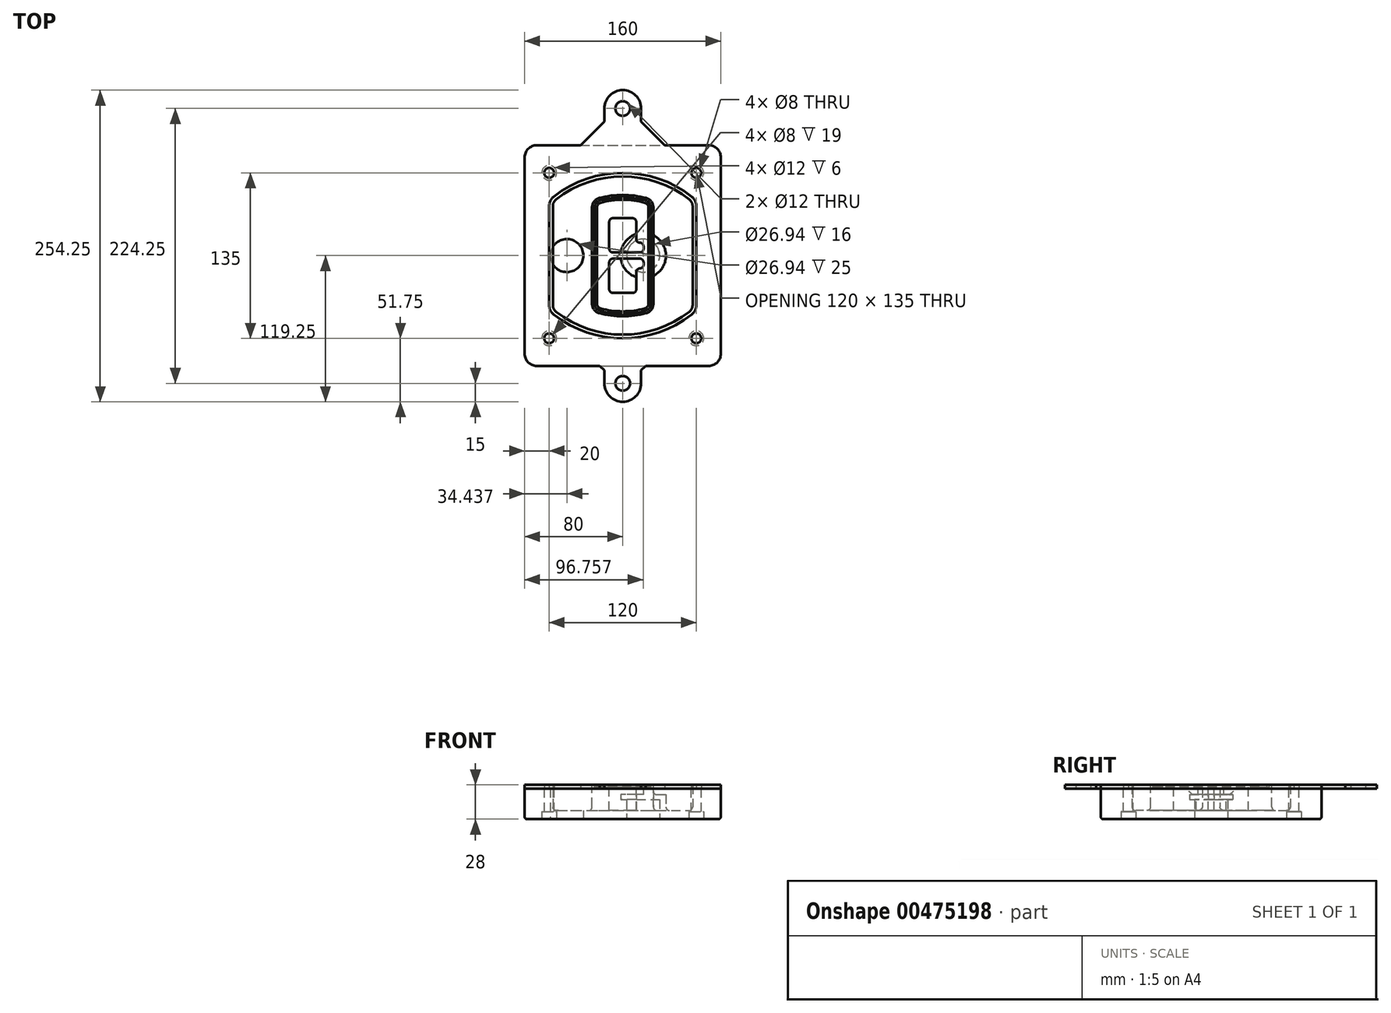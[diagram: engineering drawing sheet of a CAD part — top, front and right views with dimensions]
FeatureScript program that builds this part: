
annotation { "Feature Type Name" : "Feature", "Feature Type Description" : "" }
export const myFeature = defineFeature(function(context is Context, id is Id, definition is map)
    precondition{}
    {
        {
            var Q0;
            Q0=qCreatedBy(makeId("Top.planeOp"),FACE);
            var sketch = newSketch(context, id + "F0", { "sketchPlane" : qUnion([Q0])});
            skPoint(sketch, "E0.rect.middle", {"position": v(0, 0) * mm});
            skLineSegment(sketch, "E1.bottom", {"start": v(-70, -90) * mm, "end": v(70, -90) * mm});
            skLineSegment(sketch, "E1.top", {"start": v(-70, 90) * mm, "end": v(70, 90) * mm});
            skLineSegment(sketch, "E1.left", {"start": v(-80, -80) * mm, "end": v(-80, 80) * mm});
            skLineSegment(sketch, "E1.right", {"start": v(80, -80) * mm, "end": v(80, 80) * mm});
            skLineSegment(sketch, "E2", {"start": v(-80, 90) * mm, "end": v(80, -90) * mm, "construction": true});
            skLineSegment(sketch, "E3", {"start": v(80, 90) * mm, "end": v(-80, -90) * mm, "construction": true});
            skCircle(sketch, "E4", {"center": v(-60, 67.5) * mm, "radius": 4 * mm});
            skCircle(sketch, "E5", {"center": v(60, 67.5) * mm, "radius": 4 * mm});
            skCircle(sketch, "E6", {"center": v(60, -67.5) * mm, "radius": 4 * mm});
            skCircle(sketch, "E7", {"center": v(-60, -67.5) * mm, "radius": 4 * mm});
            skLineSegment(sketch, "E8", {"start": v(-60, 67.5) * mm, "end": v(60, 67.5) * mm, "construction": true});
            skLineSegment(sketch, "E9", {"start": v(60, 67.5) * mm, "end": v(60, -67.5) * mm, "construction": true});
            skLineSegment(sketch, "E10", {"start": v(60, -67.5) * mm, "end": v(-60, -67.5) * mm, "construction": true});
            skLineSegment(sketch, "E11", {"start": v(-60, -67.5) * mm, "end": v(-60, 67.5) * mm, "construction": true});
            skLineSegment(sketch, "E12", {"start": v(-60, 40.3) * mm, "end": v(-60, -40.3) * mm});
            skLineSegment(sketch, "E13", {"start": v(60, 40.3) * mm, "end": v(60, -40.3) * mm});
            skArc(sketch, "E14", {"start": v(56.15, 48.18) * mm, "mid": v(0, 67.5) * mm, "end": v(-56.15, 48.18) * mm});
            skArc(sketch, "E15", {"start": v(-56.15, -48.18) * mm, "mid": v(0, -67.5) * mm, "end": v(56.15, -48.18) * mm});
            skLineSegment(sketch, "E16", {"start": v(-60, 0) * mm, "end": v(60, 0) * mm, "construction": true});
            skPoint(sketch, "E17.visualSharp", {"position": v(-60, -45) * mm});
            skArc(sketch, "E17.filletArc", {"start": v(-60, -40.3) * mm, "mid": v(-58.99, -44.68) * mm, "end": v(-56.15, -48.18) * mm});
            skPoint(sketch, "E18.visualSharp", {"position": v(-60, 45) * mm});
            skArc(sketch, "E18.filletArc", {"start": v(-56.15, 48.18) * mm, "mid": v(-58.99, 44.68) * mm, "end": v(-60, 40.3) * mm});
            skPoint(sketch, "E19.visualSharp", {"position": v(60, 45) * mm});
            skArc(sketch, "E19.filletArc", {"start": v(60, 40.3) * mm, "mid": v(58.99, 44.68) * mm, "end": v(56.15, 48.18) * mm});
            skPoint(sketch, "E20.visualSharp", {"position": v(60, -45) * mm});
            skArc(sketch, "E20.filletArc", {"start": v(56.15, -48.18) * mm, "mid": v(58.99, -44.68) * mm, "end": v(60, -40.3) * mm});
            skPoint(sketch, "E21.visualSharp", {"position": v(-80, 90) * mm});
            skArc(sketch, "E21.filletArc", {"start": v(-70, 90) * mm, "mid": v(-77.07, 87.07) * mm, "end": v(-80, 80) * mm});
            skPoint(sketch, "E22.visualSharp", {"position": v(80, 90) * mm});
            skArc(sketch, "E22.filletArc", {"start": v(80, 80) * mm, "mid": v(77.07, 87.07) * mm, "end": v(70, 90) * mm});
            skPoint(sketch, "E23.visualSharp", {"position": v(80, -90) * mm});
            skArc(sketch, "E23.filletArc", {"start": v(70, -90) * mm, "mid": v(77.07, -87.07) * mm, "end": v(80, -80) * mm});
            skPoint(sketch, "E24.visualSharp", {"position": v(-80, -90) * mm});
            skArc(sketch, "E24.filletArc", {"start": v(-80, -80) * mm, "mid": v(-77.07, -87.07) * mm, "end": v(-70, -90) * mm});
            skArc(sketch, "E25.0", {"start": v(57, 40.3) * mm, "mid": v(56.3, 43.36) * mm, "end": v(54.3, 45.81) * mm});
            skLineSegment(sketch, "E25.1", {"start": v(57, 40.3) * mm, "end": v(57, -40.3) * mm});
            skArc(sketch, "E25.2", {"start": v(54.3, -45.81) * mm, "mid": v(56.3, -43.36) * mm, "end": v(57, -40.3) * mm});
            skArc(sketch, "E25.3", {"start": v(-54.3, -45.81) * mm, "mid": v(0, -64.5) * mm, "end": v(54.3, -45.81) * mm});
            skArc(sketch, "E25.4", {"start": v(-57, -40.3) * mm, "mid": v(-56.3, -43.36) * mm, "end": v(-54.3, -45.81) * mm});
            skArc(sketch, "E25.5", {"start": v(54.3, 45.81) * mm, "mid": v(0, 64.5) * mm, "end": v(-54.3, 45.81) * mm});
            skLineSegment(sketch, "E25.6", {"start": v(-57, 40.3) * mm, "end": v(-57, -40.3) * mm});
            skArc(sketch, "E25.7", {"start": v(-54.3, 45.81) * mm, "mid": v(-56.3, 43.36) * mm, "end": v(-57, 40.3) * mm});
            skArc(sketch, "E26.0", {"start": v(-58.62, 51.33) * mm, "mid": v(-62.58, 46.43) * mm, "end": v(-64, 40.3) * mm});
            skArc(sketch, "E26.1", {"start": v(58.62, 51.33) * mm, "mid": v(0, 71.5) * mm, "end": v(-58.62, 51.33) * mm});
            skArc(sketch, "E26.2", {"start": v(64, 40.3) * mm, "mid": v(62.58, 46.43) * mm, "end": v(58.62, 51.33) * mm});
            skLineSegment(sketch, "E26.3", {"start": v(64, 40.3) * mm, "end": v(64, -40.3) * mm});
            skArc(sketch, "E26.4", {"start": v(58.62, -51.33) * mm, "mid": v(62.58, -46.43) * mm, "end": v(64, -40.3) * mm});
            skLineSegment(sketch, "E26.5", {"start": v(-64, 40.3) * mm, "end": v(-64, -40.3) * mm});
            skArc(sketch, "E26.6", {"start": v(-58.62, -51.33) * mm, "mid": v(0, -71.5) * mm, "end": v(58.62, -51.33) * mm});
            skArc(sketch, "E26.7", {"start": v(-64, -40.3) * mm, "mid": v(-62.58, -46.43) * mm, "end": v(-58.62, -51.33) * mm});
            skSolve(sketch);
        }
        {
            var Q0;
            Q0=makeQuery(id+"F0.imprint","IMPRINT",FACE,{"disambiguationData":[TD([[makeQuery(id+"F0.imprint","IMPRINT",EDGE,{"derivedFrom":sQuery(id+"F0.wireOp",EDGE,"E1.bottom")}),1.0]])]});
            var Q1;
            Q1=makeQuery(id+"F0.imprint","IMPRINT",FACE,{"disambiguationData":[TD([[makeQuery(id+"F0.imprint","IMPRINT",EDGE,{"derivedFrom":sQuery(id+"F0.wireOp",EDGE,"E12")}),1.0]])]});
            var Q2;
            Q2=makeQuery(id+"F0.imprint","IMPRINT",FACE,{"disambiguationData":[TD([[makeQuery(id+"F0.imprint","IMPRINT",EDGE,{"derivedFrom":sQuery(id+"F0.wireOp",EDGE,"E25.0")}),1.0]])]});
            var Q3;
            Q3=makeQuery(id+"F0.imprint","IMPRINT",FACE,{"disambiguationData":[TD([[makeQuery(id+"F0.imprint","IMPRINT",EDGE,{"derivedFrom":sQuery(id+"F0.wireOp",EDGE,"E12")}),-1.0]])]});
            extrude(context, id + "F1", {"entities" : qUnion([Q0, Q1, Q2, Q3]), "oppositeDirection" : true, "depth" : 25 * mm});
        }
        {
            var Q0;
            Q0=makeQuery(id+"F0.imprint","IMPRINT",FACE,{"disambiguationData":[TD([[makeQuery(id+"F0.imprint","IMPRINT",EDGE,{"derivedFrom":sQuery(id+"F0.wireOp",EDGE,"E12")}),1.0]])]});
            extrude(context, id + "F2", {"entities" : qUnion([Q0]), "operationType" : NewBodyOperationType.ADD, "depth" : 3 * mm});
        }
        {
            var Q0;
            Q0=makeQuery(id+"F0.imprint","IMPRINT",FACE,{"disambiguationData":[TD([[makeQuery(id+"F0.imprint","IMPRINT",EDGE,{"derivedFrom":sQuery(id+"F0.wireOp",EDGE,"E25.0")}),1.0]])]});
            extrude(context, id + "F3", {"entities" : qUnion([Q0]), "operationType" : NewBodyOperationType.REMOVE, "oppositeDirection" : true, "depth" : 18 * mm});
        }
        {
            var Q0;
            Q0=makeQuery(id+"F2.opExtrude","CAP_FACE",FACE,{"disambiguationData":[OSD([sQuery(id+"F0.wireOp",EDGE,"E12"),sQuery(id+"F0.wireOp",EDGE,"E13"),sQuery(id+"F0.wireOp",EDGE,"E14"),sQuery(id+"F0.wireOp",EDGE,"E15"),sQuery(id+"F0.wireOp",EDGE,"E17.filletArc"),sQuery(id+"F0.wireOp",EDGE,"E18.filletArc"),sQuery(id+"F0.wireOp",EDGE,"E19.filletArc"),sQuery(id+"F0.wireOp",EDGE,"E20.filletArc"),sQuery(id+"F0.wireOp",EDGE,"E25.0"),sQuery(id+"F0.wireOp",EDGE,"E25.1"),sQuery(id+"F0.wireOp",EDGE,"E25.2"),sQuery(id+"F0.wireOp",EDGE,"E25.3"),sQuery(id+"F0.wireOp",EDGE,"E25.4"),sQuery(id+"F0.wireOp",EDGE,"E25.5"),sQuery(id+"F0.wireOp",EDGE,"E25.6"),sQuery(id+"F0.wireOp",EDGE,"E25.7")])],"isStart":false});
            var sketch = newSketch(context, id + "F4", { "sketchPlane" : qUnion([Q0])});
            skArc(sketch, "E27.0", {"start": v(-19.08, -46.97) * mm, "mid": v(0, -49.5) * mm, "end": v(19.08, -46.97) * mm});
            skArc(sketch, "E28.0", {"start": v(19.08, 46.97) * mm, "mid": v(0, 49.5) * mm, "end": v(-19.08, 46.97) * mm});
            skLineSegment(sketch, "E29", {"start": v(-25, 39.25) * mm, "end": v(-25, -39.25) * mm});
            skLineSegment(sketch, "E30", {"start": v(25, 39.25) * mm, "end": v(25, -39.25) * mm});
            skLineSegment(sketch, "E31", {"start": v(-25, 45.1) * mm, "end": v(25, 45.1) * mm, "construction": true});
            skLineSegment(sketch, "E32", {"start": v(-25, -45.1) * mm, "end": v(25, -45.1) * mm, "construction": true});
            skPoint(sketch, "E33.visualSharp", {"position": v(-25, 45.1) * mm});
            skArc(sketch, "E33.filletArc", {"start": v(-19.08, 46.97) * mm, "mid": v(-23.35, 44.11) * mm, "end": v(-25, 39.25) * mm});
            skPoint(sketch, "E34.visualSharp", {"position": v(25, 45.1) * mm});
            skArc(sketch, "E34.filletArc", {"start": v(25, 39.25) * mm, "mid": v(23.35, 44.11) * mm, "end": v(19.08, 46.97) * mm});
            skPoint(sketch, "E35.visualSharp", {"position": v(25, -45.1) * mm});
            skArc(sketch, "E35.filletArc", {"start": v(19.08, -46.97) * mm, "mid": v(23.35, -44.11) * mm, "end": v(25, -39.25) * mm});
            skPoint(sketch, "E36.visualSharp", {"position": v(-25, -45.1) * mm});
            skArc(sketch, "E36.filletArc", {"start": v(-25, -39.25) * mm, "mid": v(-23.35, -44.11) * mm, "end": v(-19.08, -46.97) * mm});
            skArc(sketch, "E37.0", {"start": v(54.3, 45.81) * mm, "mid": v(0, 64.5) * mm, "end": v(-54.3, 45.81) * mm});
            skArc(sketch, "E37.1", {"start": v(-54.3, 45.81) * mm, "mid": v(-56.3, 43.36) * mm, "end": v(-57, 40.3) * mm});
            skLineSegment(sketch, "E37.2", {"start": v(-57, 40.3) * mm, "end": v(-57, -40.3) * mm});
            skArc(sketch, "E37.3", {"start": v(-57, -40.3) * mm, "mid": v(-56.3, -43.36) * mm, "end": v(-54.3, -45.81) * mm});
            skArc(sketch, "E37.4", {"start": v(-54.3, -45.81) * mm, "mid": v(0, -64.5) * mm, "end": v(54.3, -45.81) * mm});
            skArc(sketch, "E37.5", {"start": v(54.3, -45.81) * mm, "mid": v(56.3, -43.36) * mm, "end": v(57, -40.3) * mm});
            skLineSegment(sketch, "E37.6", {"start": v(57, 40.3) * mm, "end": v(57, -40.3) * mm});
            skArc(sketch, "E37.7", {"start": v(57, 40.3) * mm, "mid": v(56.3, 43.36) * mm, "end": v(54.3, 45.81) * mm});
            skLineSegment(sketch, "E38.0", {"start": v(23, 39.25) * mm, "end": v(23, -39.25) * mm});
            skArc(sketch, "E38.1", {"start": v(18.56, -45.04) * mm, "mid": v(21.76, -42.9) * mm, "end": v(23, -39.25) * mm});
            skArc(sketch, "E38.2", {"start": v(-18.56, -45.04) * mm, "mid": v(0, -47.5) * mm, "end": v(18.56, -45.04) * mm});
            skArc(sketch, "E38.3", {"start": v(-23, -39.25) * mm, "mid": v(-21.76, -42.9) * mm, "end": v(-18.56, -45.04) * mm});
            skLineSegment(sketch, "E38.4", {"start": v(-23, 39.25) * mm, "end": v(-23, -39.25) * mm});
            skArc(sketch, "E38.5", {"start": v(23, 39.25) * mm, "mid": v(21.76, 42.9) * mm, "end": v(18.56, 45.04) * mm});
            skArc(sketch, "E38.6", {"start": v(-18.56, 45.04) * mm, "mid": v(-21.76, 42.9) * mm, "end": v(-23, 39.25) * mm});
            skArc(sketch, "E38.7", {"start": v(18.56, 45.04) * mm, "mid": v(0, 47.5) * mm, "end": v(-18.56, 45.04) * mm});
            skArc(sketch, "E39.0", {"start": v(21, 39.25) * mm, "mid": v(20.18, 41.68) * mm, "end": v(18.04, 43.1) * mm});
            skLineSegment(sketch, "E39.1", {"start": v(21, 39.25) * mm, "end": v(21, -39.25) * mm});
            skArc(sketch, "E39.2", {"start": v(18.04, -43.1) * mm, "mid": v(20.18, -41.68) * mm, "end": v(21, -39.25) * mm});
            skArc(sketch, "E39.3", {"start": v(-18.04, -43.1) * mm, "mid": v(0, -45.5) * mm, "end": v(18.04, -43.1) * mm});
            skArc(sketch, "E39.4", {"start": v(-21, -39.25) * mm, "mid": v(-20.18, -41.68) * mm, "end": v(-18.04, -43.1) * mm});
            skArc(sketch, "E39.5", {"start": v(18.04, 43.1) * mm, "mid": v(0, 45.5) * mm, "end": v(-18.04, 43.1) * mm});
            skLineSegment(sketch, "E39.6", {"start": v(-21, 39.25) * mm, "end": v(-21, -39.25) * mm});
            skArc(sketch, "E39.7", {"start": v(-18.04, 43.1) * mm, "mid": v(-20.18, 41.68) * mm, "end": v(-21, 39.25) * mm});
            skLineSegment(sketch, "E40", {"start": v(-25, 0) * mm, "end": v(25, 0) * mm, "construction": true});
            skLineSegment(sketch, "E41", {"start": v(-11, 5.5) * mm, "end": v(-11, 27.5) * mm});
            skLineSegment(sketch, "E42", {"start": v(-8, 30.5) * mm, "end": v(8, 30.5) * mm});
            skLineSegment(sketch, "E43", {"start": v(11, 27.5) * mm, "end": v(11, 13.5) * mm});
            skLineSegment(sketch, "E44", {"start": v(14, 10.5) * mm, "end": v(14, 10.5) * mm});
            skLineSegment(sketch, "E45", {"start": v(17, 7.5) * mm, "end": v(17, 5.5) * mm});
            skLineSegment(sketch, "E46", {"start": v(14, 2.5) * mm, "end": v(-8, 2.5) * mm});
            skPoint(sketch, "E47.visualSharp", {"position": v(-11, 30.5) * mm});
            skArc(sketch, "E47.filletArc", {"start": v(-8, 30.5) * mm, "mid": v(-10.12, 29.62) * mm, "end": v(-11, 27.5) * mm});
            skPoint(sketch, "E48.visualSharp", {"position": v(11, 30.5) * mm});
            skArc(sketch, "E48.filletArc", {"start": v(11, 27.5) * mm, "mid": v(10.12, 29.62) * mm, "end": v(8, 30.5) * mm});
            skPoint(sketch, "E49.visualSharp", {"position": v(11, 10.5) * mm});
            skArc(sketch, "E49.filletArc", {"start": v(11, 13.5) * mm, "mid": v(11.88, 11.38) * mm, "end": v(14, 10.5) * mm});
            skPoint(sketch, "E50.visualSharp", {"position": v(17, 10.5) * mm});
            skArc(sketch, "E50.filletArc", {"start": v(17, 7.5) * mm, "mid": v(16.12, 9.62) * mm, "end": v(14, 10.5) * mm});
            skPoint(sketch, "E51.visualSharp", {"position": v(17, 2.5) * mm});
            skArc(sketch, "E51.filletArc", {"start": v(14, 2.5) * mm, "mid": v(16.12, 3.38) * mm, "end": v(17, 5.5) * mm});
            skPoint(sketch, "E52.visualSharp", {"position": v(-11, 2.5) * mm});
            skArc(sketch, "E52.filletArc", {"start": v(-11, 5.5) * mm, "mid": v(-10.12, 3.38) * mm, "end": v(-8, 2.5) * mm});
            skLineSegment(sketch, "E53.0.MirrorCS", {"start": v(14, -2.5) * mm, "end": v(-8, -2.5) * mm});
            skArc(sketch, "E54.0.MirrorCS", {"start": v(-11, -5.5) * mm, "mid": v(-10.12, -3.38) * mm, "end": v(-8, -2.5) * mm});
            skLineSegment(sketch, "E55.0.MirrorCS", {"start": v(-11, -5.5) * mm, "end": v(-11, -27.5) * mm});
            skArc(sketch, "E56.0.MirrorCS", {"start": v(-8, -30.5) * mm, "mid": v(-10.12, -29.62) * mm, "end": v(-11, -27.5) * mm});
            skLineSegment(sketch, "E57.0.MirrorCS", {"start": v(-8, -30.5) * mm, "end": v(8, -30.5) * mm});
            skArc(sketch, "E58.0.MirrorCS", {"start": v(11, -27.5) * mm, "mid": v(10.12, -29.62) * mm, "end": v(8, -30.5) * mm});
            skLineSegment(sketch, "E59.0.MirrorCS", {"start": v(11, -27.5) * mm, "end": v(11, -13.5) * mm});
            skArc(sketch, "E60.0.MirrorCS", {"start": v(11, -13.5) * mm, "mid": v(11.88, -11.38) * mm, "end": v(14, -10.5) * mm});
            skArc(sketch, "E61.0.MirrorCS", {"start": v(17, -7.5) * mm, "mid": v(16.12, -9.62) * mm, "end": v(14, -10.5) * mm});
            skLineSegment(sketch, "E62.0.MirrorCS", {"start": v(17, -7.5) * mm, "end": v(17, -5.5) * mm});
            skArc(sketch, "E63.0.MirrorCS", {"start": v(14, -2.5) * mm, "mid": v(16.12, -3.38) * mm, "end": v(17, -5.5) * mm});
            skSolve(sketch);
        }
        {
            var Q0;
            Q0=makeQuery(id+"F4.imprint","IMPRINT",FACE,{"disambiguationData":[TD([[makeQuery(id+"F4.imprint","IMPRINT",EDGE,{"derivedFrom":sQuery(id+"F4.wireOp",EDGE,"E27.0")}),1.0]])]});
            var Q1;
            Q1=makeQuery(id+"F4.imprint","IMPRINT",FACE,{"disambiguationData":[TD([[makeQuery(id+"F4.imprint","IMPRINT",EDGE,{"derivedFrom":sQuery(id+"F4.wireOp",EDGE,"E38.0")}),-1.0]])]});
            var Q2;
            Q2=makeQuery(id+"F4.imprint","IMPRINT",FACE,{"disambiguationData":[TD([[makeQuery(id+"F4.imprint","IMPRINT",EDGE,{"derivedFrom":sQuery(id+"F4.wireOp",EDGE,"E39.0")}),1.0]])]});
            extrude(context, id + "F5", {"entities" : qUnion([Q0, Q1, Q2]), "operationType" : NewBodyOperationType.ADD, "endBound" : BoundingType.UP_TO_NEXT, "oppositeDirection" : true, "depth" : 25 * mm});
        }
        {
            var Q0;
            Q0=makeQuery(id+"F4.imprint","IMPRINT",FACE,{"disambiguationData":[TD([[makeQuery(id+"F4.imprint","IMPRINT",EDGE,{"derivedFrom":sQuery(id+"F4.wireOp",EDGE,"E38.0")}),-1.0]])]});
            extrude(context, id + "F6", {"entities" : qUnion([Q0]), "operationType" : NewBodyOperationType.REMOVE, "oppositeDirection" : true, "depth" : 2 * mm});
        }
        {
            var Q0;
            Q0=makeQuery(id+"F1.opExtrude","CAP_FACE",FACE,{"disambiguationData":[OSD([sQuery(id+"F0.wireOp",EDGE,"E1.bottom"),sQuery(id+"F0.wireOp",EDGE,"E1.top"),sQuery(id+"F0.wireOp",EDGE,"E1.left"),sQuery(id+"F0.wireOp",EDGE,"E1.right"),sQuery(id+"F0.wireOp",EDGE,"E4"),sQuery(id+"F0.wireOp",EDGE,"E5"),sQuery(id+"F0.wireOp",EDGE,"E6"),sQuery(id+"F0.wireOp",EDGE,"E7"),sQuery(id+"F0.wireOp",EDGE,"E21.filletArc"),sQuery(id+"F0.wireOp",EDGE,"E22.filletArc"),sQuery(id+"F0.wireOp",EDGE,"E23.filletArc"),sQuery(id+"F0.wireOp",EDGE,"E24.filletArc")])],"isStart":false});
            var sketch = newSketch(context, id + "F7", { "sketchPlane" : qUnion([Q0])});
            skCircle(sketch, "E64", {"center": v(16.76, 0) * mm, "radius": 13.47 * mm});
            skCircle(sketch, "E65", {"center": v(-45.56, 0) * mm, "radius": 13.47 * mm});
            skLineSegment(sketch, "E66", {"start": v(80, 0) * mm, "end": v(-80, 0) * mm});
            skCircle(sketch, "E67", {"center": v(16.76, 0) * mm, "radius": 18.47 * mm});
            skCircle(sketch, "E68", {"center": v(60, -67.5) * mm, "radius": 6 * mm});
            skCircle(sketch, "E69", {"center": v(-60, -67.5) * mm, "radius": 6 * mm});
            skCircle(sketch, "E70", {"center": v(-60, 67.5) * mm, "radius": 6 * mm});
            skCircle(sketch, "E71", {"center": v(60, 67.5) * mm, "radius": 6 * mm});
            skSolve(sketch);
        }
        {
            var Q0;
            {var subQ1=sQuery(id+"F7.wireOp",EDGE,"E66");var subQ4=sQuery(id+"F7.wireOp",EDGE,"E64");var subQ6=makeQuery(id+"F7.imprint","INTERSECT",VERTEX,{"disambiguationData":[OD(0.0)],"derivedFrom":[subQ4,subQ1]});Q0=makeQuery(id+"F7.imprint","IMPRINT",FACE,{"disambiguationData":[TD([[makeQuery(id+"F7.imprint","IMPRINT",EDGE,{"disambiguationData":[TD([[subQ6,-1.0]])],"derivedFrom":subQ4}),-1.0]])]});}
            var Q1;
            {var subQ0=sQuery(id+"F7.wireOp",EDGE,"E66");var subQ1=sQuery(id+"F7.wireOp",EDGE,"E64");var subQ3=makeQuery(id+"F7.imprint","INTERSECT",VERTEX,{"disambiguationData":[OD(0.0)],"derivedFrom":[subQ1,subQ0]});Q1=makeQuery(id+"F7.imprint","IMPRINT",FACE,{"disambiguationData":[TD([[makeQuery(id+"F7.imprint","IMPRINT",EDGE,{"disambiguationData":[TD([[subQ3,-1.0]])],"derivedFrom":subQ1}),1.0]])]});}
            var Q2;
            {var subQ0=sQuery(id+"F7.wireOp",EDGE,"E66");var subQ1=sQuery(id+"F7.wireOp",EDGE,"E64");var subQ3=makeQuery(id+"F7.imprint","INTERSECT",VERTEX,{"disambiguationData":[OD(0.0)],"derivedFrom":[subQ1,subQ0]});Q2=makeQuery(id+"F7.imprint","IMPRINT",FACE,{"disambiguationData":[TD([[makeQuery(id+"F7.imprint","IMPRINT",EDGE,{"disambiguationData":[TD([[subQ3,1.0]])],"derivedFrom":subQ1}),1.0]])]});}
            var Q3;
            {var subQ1=sQuery(id+"F7.wireOp",EDGE,"E66");var subQ4=sQuery(id+"F7.wireOp",EDGE,"E64");var subQ6=makeQuery(id+"F7.imprint","INTERSECT",VERTEX,{"disambiguationData":[OD(0.0)],"derivedFrom":[subQ4,subQ1]});Q3=makeQuery(id+"F7.imprint","IMPRINT",FACE,{"disambiguationData":[TD([[makeQuery(id+"F7.imprint","IMPRINT",EDGE,{"disambiguationData":[TD([[subQ6,1.0]])],"derivedFrom":subQ4}),-1.0]])]});}
            extrude(context, id + "F8", {"entities" : qUnion([Q0, Q1, Q2, Q3]), "operationType" : NewBodyOperationType.ADD, "oppositeDirection" : true, "depth" : 20 * mm});
        }
        {
            var Q0;
            {var subQ0=sQuery(id+"F7.wireOp",EDGE,"E66");var subQ1=sQuery(id+"F7.wireOp",EDGE,"E64");var subQ3=makeQuery(id+"F7.imprint","INTERSECT",VERTEX,{"disambiguationData":[OD(0.0)],"derivedFrom":[subQ1,subQ0]});Q0=makeQuery(id+"F7.imprint","IMPRINT",FACE,{"disambiguationData":[TD([[makeQuery(id+"F7.imprint","IMPRINT",EDGE,{"disambiguationData":[TD([[subQ3,-1.0]])],"derivedFrom":subQ1}),1.0]])]});}
            var Q1;
            {var subQ0=sQuery(id+"F7.wireOp",EDGE,"E66");var subQ1=sQuery(id+"F7.wireOp",EDGE,"E64");var subQ3=makeQuery(id+"F7.imprint","INTERSECT",VERTEX,{"disambiguationData":[OD(0.0)],"derivedFrom":[subQ1,subQ0]});Q1=makeQuery(id+"F7.imprint","IMPRINT",FACE,{"disambiguationData":[TD([[makeQuery(id+"F7.imprint","IMPRINT",EDGE,{"disambiguationData":[TD([[subQ3,1.0]])],"derivedFrom":subQ1}),1.0]])]});}
            extrude(context, id + "F9", {"entities" : qUnion([Q0, Q1]), "operationType" : NewBodyOperationType.REMOVE, "oppositeDirection" : true, "depth" : 16 * mm});
        }
        {
            var Q0;
            {var subQ0=sQuery(id+"F7.wireOp",EDGE,"E66");var subQ1=sQuery(id+"F7.wireOp",EDGE,"E65");var subQ3=makeQuery(id+"F7.imprint","INTERSECT",VERTEX,{"disambiguationData":[OD(0.0)],"derivedFrom":[subQ1,subQ0]});Q0=makeQuery(id+"F7.imprint","IMPRINT",FACE,{"disambiguationData":[TD([[makeQuery(id+"F7.imprint","IMPRINT",EDGE,{"disambiguationData":[TD([[subQ3,-1.0]])],"derivedFrom":subQ1}),1.0]])]});}
            var Q1;
            {var subQ0=sQuery(id+"F7.wireOp",EDGE,"E66");var subQ1=sQuery(id+"F7.wireOp",EDGE,"E65");var subQ3=makeQuery(id+"F7.imprint","INTERSECT",VERTEX,{"disambiguationData":[OD(0.0)],"derivedFrom":[subQ1,subQ0]});Q1=makeQuery(id+"F7.imprint","IMPRINT",FACE,{"disambiguationData":[TD([[makeQuery(id+"F7.imprint","IMPRINT",EDGE,{"disambiguationData":[TD([[subQ3,1.0]])],"derivedFrom":subQ1}),1.0]])]});}
            extrude(context, id + "F10", {"entities" : qUnion([Q0, Q1]), "operationType" : NewBodyOperationType.REMOVE, "oppositeDirection" : true, "depth" : 25 * mm});
        }
        {
            var Q0;
            Q0=makeQuery(id+"F7.imprint","IMPRINT",FACE,{"disambiguationData":[TD([[makeQuery(id+"F7.imprint","IMPRINT",EDGE,{"derivedFrom":sQuery(id+"F7.wireOp",EDGE,"E68")}),1.0]])]});
            var Q1;
            Q1=makeQuery(id+"F7.imprint","IMPRINT",FACE,{"disambiguationData":[TD([[makeQuery(id+"F7.imprint","IMPRINT",EDGE,{"derivedFrom":makeQuery(id+"F1.opExtrude","CAP_EDGE",EDGE,{"disambiguationData":[OSD([sQuery(id+"F0.wireOp",EDGE,"E5")])],"isStart":false})}),-1.0]])]});
            var Q2;
            Q2=makeQuery(id+"F7.imprint","IMPRINT",FACE,{"disambiguationData":[TD([[makeQuery(id+"F7.imprint","IMPRINT",EDGE,{"derivedFrom":sQuery(id+"F7.wireOp",EDGE,"E69")}),1.0]])]});
            var Q3;
            Q3=makeQuery(id+"F7.imprint","IMPRINT",FACE,{"disambiguationData":[TD([[makeQuery(id+"F7.imprint","IMPRINT",EDGE,{"derivedFrom":makeQuery(id+"F1.opExtrude","CAP_EDGE",EDGE,{"disambiguationData":[OSD([sQuery(id+"F0.wireOp",EDGE,"E4")])],"isStart":false})}),-1.0]])]});
            var Q4;
            Q4=makeQuery(id+"F7.imprint","IMPRINT",FACE,{"disambiguationData":[TD([[makeQuery(id+"F7.imprint","IMPRINT",EDGE,{"derivedFrom":sQuery(id+"F7.wireOp",EDGE,"E70")}),1.0]])]});
            var Q5;
            Q5=makeQuery(id+"F7.imprint","IMPRINT",FACE,{"disambiguationData":[TD([[makeQuery(id+"F7.imprint","IMPRINT",EDGE,{"derivedFrom":makeQuery(id+"F1.opExtrude","CAP_EDGE",EDGE,{"disambiguationData":[OSD([sQuery(id+"F0.wireOp",EDGE,"E7")])],"isStart":false})}),-1.0]])]});
            var Q6;
            Q6=makeQuery(id+"F7.imprint","IMPRINT",FACE,{"disambiguationData":[TD([[makeQuery(id+"F7.imprint","IMPRINT",EDGE,{"derivedFrom":sQuery(id+"F7.wireOp",EDGE,"E71")}),1.0]])]});
            var Q7;
            Q7=makeQuery(id+"F7.imprint","IMPRINT",FACE,{"disambiguationData":[TD([[makeQuery(id+"F7.imprint","IMPRINT",EDGE,{"derivedFrom":makeQuery(id+"F1.opExtrude","CAP_EDGE",EDGE,{"disambiguationData":[OSD([sQuery(id+"F0.wireOp",EDGE,"E6")])],"isStart":false})}),-1.0]])]});
            extrude(context, id + "F11", {"entities" : qUnion([Q0, Q1, Q2, Q3, Q4, Q5, Q6, Q7]), "operationType" : NewBodyOperationType.REMOVE, "oppositeDirection" : true, "depth" : 6 * mm});
        }
        {
            var Q0;
            Q0=makeQuery(id+"F9.boolean.opBoolean","COPY",FACE,{"derivedFrom":makeQuery(id+"F9.opExtrude","CAP_FACE",FACE,{"disambiguationData":[OSD([sQuery(id+"F7.wireOp",EDGE,"E64")])],"isStart":false})});
            var sketch = newSketch(context, id + "F12", { "sketchPlane" : qUnion([Q0])});
            skArc(sketch, "E72.0", {"start": v(11, 17.55) * mm, "mid": v(2.57, 11.82) * mm, "end": v(-1.54, 2.5) * mm});
            skArc(sketch, "E72.1", {"start": v(-1.54, -2.5) * mm, "mid": v(2.57, -11.82) * mm, "end": v(11, -17.55) * mm});
            skLineSegment(sketch, "E73", {"start": v(-1.54, -2.5) * mm, "end": v(14, -2.5) * mm});
            skLineSegment(sketch, "E74.0", {"start": v(14, 2.5) * mm, "end": v(-1.54, 2.5) * mm});
            skArc(sketch, "E74.1", {"start": v(14, 2.5) * mm, "mid": v(16.12, 3.38) * mm, "end": v(17, 5.5) * mm});
            skLineSegment(sketch, "E74.2", {"start": v(17, 7.5) * mm, "end": v(17, 5.5) * mm});
            skArc(sketch, "E74.3", {"start": v(17, 7.5) * mm, "mid": v(16.12, 9.62) * mm, "end": v(14, 10.5) * mm});
            skArc(sketch, "E74.4", {"start": v(11, 13.5) * mm, "mid": v(11.88, 11.38) * mm, "end": v(14, 10.5) * mm});
            skLineSegment(sketch, "E74.5", {"start": v(11, 17.55) * mm, "end": v(11, 13.5) * mm});
            skLineSegment(sketch, "E74.7", {"start": v(14, -2.5) * mm, "end": v(-1.54, -2.5) * mm});
            skArc(sketch, "E74.8", {"start": v(14, -2.5) * mm, "mid": v(16.12, -3.38) * mm, "end": v(17, -5.5) * mm});
            skLineSegment(sketch, "E74.9", {"start": v(17, -7.5) * mm, "end": v(17, -5.5) * mm});
            skArc(sketch, "E74.10", {"start": v(17, -7.5) * mm, "mid": v(16.12, -9.62) * mm, "end": v(14, -10.5) * mm});
            skArc(sketch, "E74.11", {"start": v(11, -13.5) * mm, "mid": v(11.88, -11.38) * mm, "end": v(14, -10.5) * mm});
            skLineSegment(sketch, "E74.12", {"start": v(11, -17.55) * mm, "end": v(11, -13.5) * mm});
            skPoint(sketch, "E75.orphan", {"position": v(11, -27.5) * mm});
            skPoint(sketch, "E76.orphan", {"position": v(-8, -2.5) * mm});
            skPoint(sketch, "E77.orphan", {"position": v(-8, 2.5) * mm});
            skPoint(sketch, "E78.orphan", {"position": v(11, 27.5) * mm});
            skSolve(sketch);
        }
        {
            var Q0;
            {var subQ7=sQuery(id+"F12.wireOp",EDGE,"E72.0");var subQ14=sQuery(id+"F12.wireOp",EDGE,"E72.1");var subQ16=sQuery(id+"F12.wireOp",EDGE,"E74.1");var subQ18=sQuery(id+"F12.wireOp",EDGE,"E74.8");Q0=qUnion([makeQuery(id+"F12.imprint","IMPRINT",FACE,{"disambiguationData":[TD([[makeQuery(id+"F12.imprint","IMPRINT",EDGE,{"derivedFrom":subQ7}),1.0]])]}),makeQuery(id+"F12.imprint","IMPRINT",FACE,{"disambiguationData":[TD([[makeQuery(id+"F12.imprint","IMPRINT",EDGE,{"derivedFrom":subQ14}),1.0]])]}),makeQuery(id+"F12.imprint","IMPRINT",FACE,{"disambiguationData":[TD([[makeQuery(id+"F12.imprint","IMPRINT",EDGE,{"derivedFrom":subQ16}),1.0]])]}),makeQuery(id+"F12.imprint","IMPRINT",FACE,{"disambiguationData":[TD([[makeQuery(id+"F12.imprint","IMPRINT",EDGE,{"derivedFrom":subQ18}),-1.0]])]})]);}
            var Q1;
            Q1=makeQuery(id+"F5.boolean.opBoolean","SPLIT",FACE,{"disambiguationData":[TD([makeQuery(id+"F5.opExtrude","SWEPT_FACE",FACE,{"disambiguationData":[OSD([sQuery(id+"F4.wireOp",EDGE,"E41")])]})])],"derivedFrom":makeQuery(id+"F3.boolean.opBoolean","COPY",FACE,{"derivedFrom":makeQuery(id+"F3.opExtrude","CAP_FACE",FACE,{"disambiguationData":[OSD([sQuery(id+"F0.wireOp",EDGE,"E25.0"),sQuery(id+"F0.wireOp",EDGE,"E25.1"),sQuery(id+"F0.wireOp",EDGE,"E25.2"),sQuery(id+"F0.wireOp",EDGE,"E25.3"),sQuery(id+"F0.wireOp",EDGE,"E25.4"),sQuery(id+"F0.wireOp",EDGE,"E25.5"),sQuery(id+"F0.wireOp",EDGE,"E25.6"),sQuery(id+"F0.wireOp",EDGE,"E25.7")])],"isStart":false})})});
            extrude(context, id + "F13", {"entities" : qUnion([Q0]), "operationType" : NewBodyOperationType.REMOVE, "endBound" : BoundingType.UP_TO_SURFACE, "endBoundEntityFace" : qUnion([Q1]), "depth" : 25 * mm});
        }
        {
            var Q0;
            Q0=makeQuery(id+"F3.boolean.opBoolean","COPY",EDGE,{"derivedFrom":makeQuery(id+"F3.opExtrude","CAP_EDGE",EDGE,{"disambiguationData":[OSD([sQuery(id+"F0.wireOp",EDGE,"E25.6")])],"isStart":false})});
            var Q1;
            Q1=makeQuery(id+"F8.boolean.opBoolean","INTERSECT",EDGE,{"derivedFrom":[makeQuery(id+"F5.opExtrude","SWEPT_FACE",FACE,{"disambiguationData":[OSD([sQuery(id+"F4.wireOp",EDGE,"E30")])]}),makeQuery(id+"F8.opExtrude","CAP_FACE",FACE,{"disambiguationData":[OSD([sQuery(id+"F7.wireOp",EDGE,"E67")])],"isStart":false})]});
            var Q2;
            Q2=makeQuery(id+"F8.boolean.opBoolean","INTERSECT",EDGE,{"disambiguationData":[OD(1.0)],"derivedFrom":[makeQuery(id+"F5.opExtrude","SWEPT_FACE",FACE,{"disambiguationData":[OSD([sQuery(id+"F4.wireOp",EDGE,"E30")])]}),makeQuery(id+"F8.opExtrude","SWEPT_FACE",FACE,{"disambiguationData":[OSD([sQuery(id+"F7.wireOp",EDGE,"E67")])]})]});
            var Q3;
            {var subQ0=sQuery(id+"F4.wireOp",EDGE,"E30");Q3=makeQuery(id+"F8.boolean.opBoolean","SPLIT",EDGE,{"disambiguationData":[TD([makeQuery(id+"F5.opExtrude","SWEPT_FACE",FACE,{"disambiguationData":[OSD([sQuery(id+"F4.wireOp",EDGE,"E35.filletArc")])]})])],"derivedFrom":makeQuery(id+"F5.opExtrude","CAP_EDGE",EDGE,{"disambiguationData":[OSD([subQ0])],"isStart":false})});}
            var Q4;
            {var subQ0=sQuery(id+"F0.wireOp",EDGE,"E25.7");var subQ1=sQuery(id+"F0.wireOp",EDGE,"E25.1");var subQ2=sQuery(id+"F0.wireOp",EDGE,"E25.6");var subQ3=sQuery(id+"F0.wireOp",EDGE,"E25.5");var subQ4=sQuery(id+"F0.wireOp",EDGE,"E25.4");var subQ5=sQuery(id+"F0.wireOp",EDGE,"E25.0");var subQ6=sQuery(id+"F0.wireOp",EDGE,"E25.2");var subQ7=sQuery(id+"F0.wireOp",EDGE,"E25.3");Q4=makeQuery(id+"F8.boolean.opBoolean","INTERSECT",EDGE,{"derivedFrom":[makeQuery(id+"F5.boolean.opBoolean","SPLIT",FACE,{"disambiguationData":[TD([makeQuery(id+"F2.opExtrude","SWEPT_FACE",FACE,{"disambiguationData":[OSD([subQ5])]})])],"derivedFrom":makeQuery(id+"F3.boolean.opBoolean","COPY",FACE,{"derivedFrom":makeQuery(id+"F3.opExtrude","CAP_FACE",FACE,{"disambiguationData":[OSD([subQ5,subQ1,subQ6,subQ7,subQ4,subQ3,subQ2,subQ0])],"isStart":false})})}),makeQuery(id+"F8.opExtrude","SWEPT_FACE",FACE,{"disambiguationData":[OSD([sQuery(id+"F7.wireOp",EDGE,"E67")])]})]});}
            var Q5;
            Q5=makeQuery(id+"F8.boolean.opBoolean","INTERSECT",EDGE,{"disambiguationData":[OD(0.0)],"derivedFrom":[makeQuery(id+"F5.opExtrude","SWEPT_FACE",FACE,{"disambiguationData":[OSD([sQuery(id+"F4.wireOp",EDGE,"E30")])]}),makeQuery(id+"F8.opExtrude","SWEPT_FACE",FACE,{"disambiguationData":[OSD([sQuery(id+"F7.wireOp",EDGE,"E67")])]})]});
            fillet(context, id + "F14", {"entities" : qUnion([Q0, Q1, Q2, Q3, Q4, Q5]), "radius" : 3 * mm, "tangentPropagation" : true, "allowEdgeOverflow" : false});
        }
        {
            var Q0;
            Q0=makeQuery(id+"F1.opExtrude","CAP_EDGE",EDGE,{"disambiguationData":[OSD([sQuery(id+"F0.wireOp",EDGE,"E1.bottom")])],"isStart":false});
            fillet(context, id + "F15", {"entities" : qUnion([Q0]), "radius" : 2 * mm, "tangentPropagation" : true, "allowEdgeOverflow" : false});
        }
        {
            var Q0;
            {var subQ0=sQuery(id+"F0.wireOp",EDGE,"E21.filletArc");var subQ1=sQuery(id+"F0.wireOp",EDGE,"E7");var subQ2=sQuery(id+"F0.wireOp",EDGE,"E6");var subQ3=sQuery(id+"F0.wireOp",EDGE,"E5");var subQ4=sQuery(id+"F0.wireOp",EDGE,"E4");var subQ5=sQuery(id+"F0.wireOp",EDGE,"E22.filletArc");var subQ6=sQuery(id+"F0.wireOp",EDGE,"E1.bottom");var subQ7=sQuery(id+"F0.wireOp",EDGE,"E1.right");var subQ8=sQuery(id+"F0.wireOp",EDGE,"E1.top");var subQ9=sQuery(id+"F0.wireOp",EDGE,"E1.left");var subQ10=sQuery(id+"F0.wireOp",EDGE,"E23.filletArc");var subQ11=sQuery(id+"F0.wireOp",EDGE,"E24.filletArc");Q0=makeQuery(id+"F2.boolean.opBoolean","SPLIT",FACE,{"disambiguationData":[TD([makeQuery(id+"F1.opExtrude","SWEPT_FACE",FACE,{"disambiguationData":[OSD([subQ6])]})])],"derivedFrom":makeQuery(id+"F1.opExtrude","CAP_FACE",FACE,{"disambiguationData":[OSD([subQ6,subQ8,subQ9,subQ7,subQ4,subQ3,subQ2,subQ1,subQ0,subQ5,subQ10,subQ11])],"isStart":true})});}
            var sketch = newSketch(context, id + "F16", { "sketchPlane" : qUnion([Q0])});
            skPoint(sketch, "E79.0", {"position": v(-70, 90) * mm});
            skArc(sketch, "E79.1", {"start": v(-70, 90) * mm, "mid": v(-77.07, 87.07) * mm, "end": v(-80, 80) * mm});
            skLineSegment(sketch, "E79.2", {"start": v(-80, -80) * mm, "end": v(-80, 80) * mm});
            skLineSegment(sketch, "E79.3", {"start": v(-70, 90) * mm, "end": v(70, 90) * mm});
            skArc(sketch, "E79.4", {"start": v(80, 80) * mm, "mid": v(77.07, 87.07) * mm, "end": v(70, 90) * mm});
            skLineSegment(sketch, "E79.5", {"start": v(80, -80) * mm, "end": v(80, 80) * mm});
            skCircle(sketch, "E79.6", {"center": v(60, 67.5) * mm, "radius": 4 * mm});
            skCircle(sketch, "E79.7", {"center": v(-60, 67.5) * mm, "radius": 4 * mm});
            skCircle(sketch, "E79.8", {"center": v(-60, -67.5) * mm, "radius": 4 * mm});
            skCircle(sketch, "E79.9", {"center": v(60, -67.5) * mm, "radius": 4 * mm});
            skArc(sketch, "E79.10", {"start": v(70, -90) * mm, "mid": v(77.07, -87.07) * mm, "end": v(80, -80) * mm});
            skLineSegment(sketch, "E79.11", {"start": v(-70, -90) * mm, "end": v(70, -90) * mm});
            skArc(sketch, "E79.12", {"start": v(-80, -80) * mm, "mid": v(-77.07, -87.07) * mm, "end": v(-70, -90) * mm});
            skArc(sketch, "E79.13", {"start": v(56.15, 48.18) * mm, "mid": v(0, 67.5) * mm, "end": v(-56.15, 48.18) * mm});
            skLineSegment(sketch, "E79.14", {"start": v(-60, 40.3) * mm, "end": v(-60, -40.3) * mm});
            skLineSegment(sketch, "E79.15", {"start": v(60, 40.3) * mm, "end": v(60, -40.3) * mm});
            skArc(sketch, "E79.16", {"start": v(-56.15, -48.18) * mm, "mid": v(0, -67.5) * mm, "end": v(56.15, -48.18) * mm});
            skArc(sketch, "E79.17", {"start": v(56.15, -48.18) * mm, "mid": v(58.99, -44.68) * mm, "end": v(60, -40.3) * mm});
            skArc(sketch, "E79.18", {"start": v(60, 40.3) * mm, "mid": v(58.99, 44.68) * mm, "end": v(56.15, 48.18) * mm});
            skArc(sketch, "E79.19", {"start": v(-60, -40.3) * mm, "mid": v(-58.99, -44.68) * mm, "end": v(-56.15, -48.18) * mm});
            skArc(sketch, "E79.20", {"start": v(-56.15, 48.18) * mm, "mid": v(-58.99, 44.68) * mm, "end": v(-60, 40.3) * mm});
            skPoint(sketch, "E79.21", {"position": v(77.07, -87.07) * mm});
            skPoint(sketch, "E79.22", {"position": v(-77.07, -87.07) * mm});
            skLineSegment(sketch, "E80", {"start": v(0, 90) * mm, "end": v(0, 120) * mm, "construction": true});
            skCircle(sketch, "E81", {"center": v(0, 120) * mm, "radius": 6 * mm});
            skLineSegment(sketch, "E82", {"start": v(15, 109.4) * mm, "end": v(15, 120) * mm});
            skArc(sketch, "E83", {"start": v(15, 120) * mm, "mid": v(0, 135) * mm, "end": v(-15, 120) * mm});
            skLineSegment(sketch, "E84", {"start": v(-15, 120) * mm, "end": v(-15, 109.4) * mm});
            skLineSegment(sketch, "E85", {"start": v(-15, 109.4) * mm, "end": v(-34.4, 90) * mm});
            skLineSegment(sketch, "E86.MirrorCS", {"start": v(-15, 109.4) * mm, "end": v(-15, 120) * mm});
            skArc(sketch, "E87.MirrorCS", {"start": v(-15, 120) * mm, "mid": v(0, 135) * mm, "end": v(15, 120) * mm});
            skLineSegment(sketch, "E88.MirrorCS", {"start": v(15, 120) * mm, "end": v(15, 109.4) * mm});
            skLineSegment(sketch, "E89.MirrorCS", {"start": v(15, 109.4) * mm, "end": v(34.4, 90) * mm});
            skLineSegment(sketch, "E90.MirrorCS", {"start": v(-15, -93.66) * mm, "end": v(-34.4, -74.25) * mm});
            skLineSegment(sketch, "E91.MirrorCS", {"start": v(-15, -93.66) * mm, "end": v(-15, -104.25) * mm});
            skArc(sketch, "E92.MirrorCS", {"start": v(15, -104.25) * mm, "mid": v(0, -119.25) * mm, "end": v(-15, -104.25) * mm});
            skCircle(sketch, "E93.MirrorC", {"center": v(0, -104.25) * mm, "radius": 6 * mm});
            skLineSegment(sketch, "E94.MirrorCS", {"start": v(15, -93.66) * mm, "end": v(15, -104.25) * mm});
            skLineSegment(sketch, "E95.MirrorCS", {"start": v(15, -93.66) * mm, "end": v(34.4, -74.25) * mm});
            skLineSegment(sketch, "E96.MirrorCS", {"start": v(0, -74.25) * mm, "end": v(0, -104.25) * mm, "construction": true});
            skSolve(sketch);
        }
        {
            var Q0;
            Q0 = qSketchRegion(id + "F16", true);
            extrude(context, id + "F17", {"entities" : qUnion([Q0]), "depth" : 3 * mm});
        }
    });
